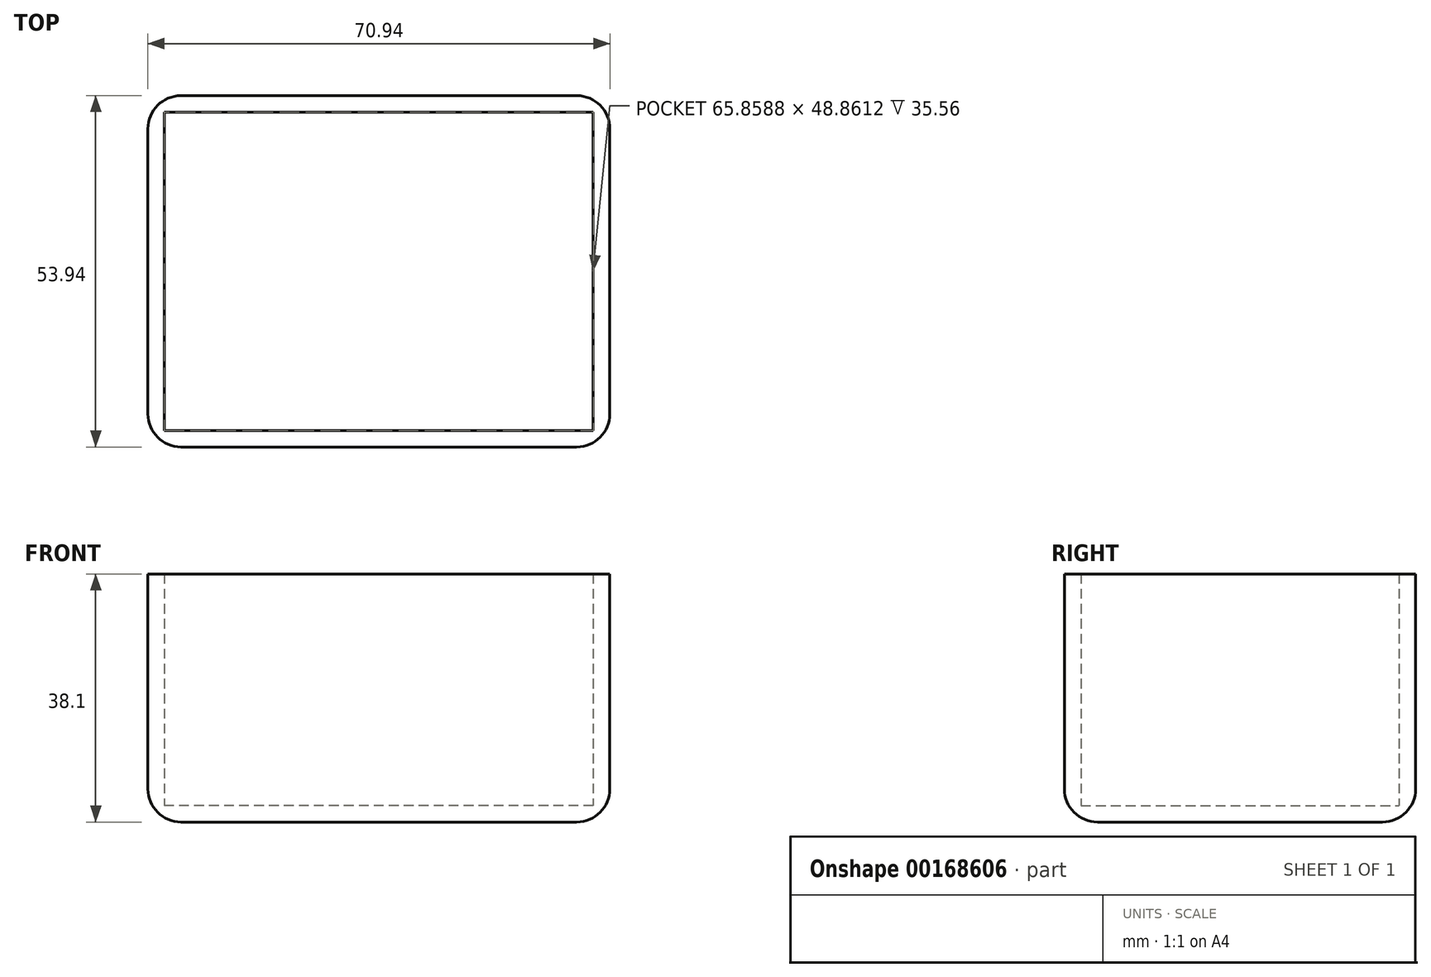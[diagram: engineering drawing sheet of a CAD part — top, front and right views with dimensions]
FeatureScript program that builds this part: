
annotation { "Feature Type Name" : "Feature", "Feature Type Description" : "" }
export const myFeature = defineFeature(function(context is Context, id is Id, definition is map)
    precondition{}
    {
        {
            var Q0;
            Q0=qCreatedBy(makeId("Top.planeOp"),FACE);
            var sketch = newSketch(context, id + "F0", { "sketchPlane" : qUnion([Q0])});
            skLineSegment(sketch, "E0.bottom", {"start": v(35.47, -26.97) * mm, "end": v(-35.47, -26.97) * mm});
            skLineSegment(sketch, "E0.top", {"start": v(35.47, 26.97) * mm, "end": v(-35.47, 26.97) * mm});
            skLineSegment(sketch, "E0.left", {"start": v(35.47, -26.97) * mm, "end": v(35.47, 26.97) * mm});
            skLineSegment(sketch, "E0.right", {"start": v(-35.47, -26.97) * mm, "end": v(-35.47, 26.97) * mm});
            skPoint(sketch, "E0.middle", {"position": v(0, 0) * mm});
            skSolve(sketch);
        }
        {
            var Q0;
            Q0=makeQuery(id+"F0.imprint","IMPRINT",FACE,{"disambiguationData":[TD([[makeQuery(id+"F0.imprint","IMPRINT",EDGE,{"derivedFrom":sQuery(id+"F0.wireOp",EDGE,"E0.bottom")}),-1.0]])]});
            extrude(context, id + "F1", {"entities" : qUnion([Q0]), "depth" : 38.1 * mm});
        }
        {
            var Q0;
            Q0=makeQuery(id+"F1.opExtrude","CAP_FACE",FACE,{"disambiguationData":[OSD([sQuery(id+"F0.wireOp",EDGE,"E0.bottom"),sQuery(id+"F0.wireOp",EDGE,"E0.top"),sQuery(id+"F0.wireOp",EDGE,"E0.left"),sQuery(id+"F0.wireOp",EDGE,"E0.right")])],"isStart":false});
            shell(context, id + "F2", {"entities" : qUnion([Q0]), "thickness" : 2.54 * mm});
        }
        {
            var Q0;
            Q0=makeQuery(id+"F1.opExtrude","CAP_EDGE",EDGE,{"disambiguationData":[OSD([sQuery(id+"F0.wireOp",EDGE,"E0.top")])],"isStart":true});
            var Q1;
            Q1=makeQuery(id+"F1.opExtrude","CAP_EDGE",EDGE,{"disambiguationData":[OSD([sQuery(id+"F0.wireOp",EDGE,"E0.bottom")])],"isStart":true});
            var Q2;
            Q2=makeQuery(id+"F1.opExtrude","SWEPT_EDGE",EDGE,{"disambiguationData":[OSD([sQuery(id+"F0.wireOp",EDGE,"E0.top"),sQuery(id+"F0.wireOp",EDGE,"E0.right")])]});
            var Q3;
            Q3=makeQuery(id+"F1.opExtrude","SWEPT_EDGE",EDGE,{"disambiguationData":[OSD([sQuery(id+"F0.wireOp",EDGE,"E0.bottom"),sQuery(id+"F0.wireOp",EDGE,"E0.left")])]});
            fillet(context, id + "F3", {"entities" : qUnion([Q0, Q1, Q2, Q3]), "radius" : 5.08 * mm, "tangentPropagation" : true, "allowEdgeOverflow" : false});
        }
        {
            var Q0;
            Q0=makeQuery(id+"F1.opExtrude","CAP_EDGE",EDGE,{"disambiguationData":[OSD([sQuery(id+"F0.wireOp",EDGE,"E0.left")])],"isStart":true});
            var Q1;
            Q1=makeQuery(id+"F1.opExtrude","CAP_EDGE",EDGE,{"disambiguationData":[OSD([sQuery(id+"F0.wireOp",EDGE,"E0.right")])],"isStart":true});
            var Q2;
            Q2=makeQuery(id+"F1.opExtrude","SWEPT_EDGE",EDGE,{"disambiguationData":[OSD([sQuery(id+"F0.wireOp",EDGE,"E0.bottom"),sQuery(id+"F0.wireOp",EDGE,"E0.right")])]});
            fillet(context, id + "F4", {"entities" : qUnion([Q0, Q1, Q2]), "radius" : 5.08 * mm, "tangentPropagation" : true, "allowEdgeOverflow" : false});
        }
    });
